# Revit family: DPD-6
name_source: partatom
category: Mechanical Equipment
revit_build: Autodesk Revit 2015 (Build: 20140606_1530(x64)
units: mm (PartAtom-declared; Revit-internal decimal feet)

## types (10) — shared parameters
Description = Drop Diffuser / Plenum
Manufacturer = United Enertech Corporation
Model = DPD-6
Type Comments = Size Options are Listed as Family Types
URL = http://unitedenertech.com

## per-type parameters (varying)
| type | B | F | Grille Height | Grille Length | T |
| DPD6-20 (8000 cfm) | 4' - 0" | 1' - 1" | 0' - 10" | 1' - 8" | 2' - 6" |
| DPD6-5 (2000 cfm) | 2' - 4" | 0' - 9" | 0' - 6" | 0' - 9" | 1' - 2" |
| DPD6-50 (20000 cfm) | 5' - 10" | 1' - 3" | 1' - 0" | 2' - 11" | 3' - 8" |
| DPD6-7.5 (3000 cfm) | 2' - 7" | 0' - 9" | 0' - 6" | 1' - 0" | 1' - 6" |
| DPD6-10 (4000 cfm) | 3' - 6" | 0' - 9" | 0' - 6" | 1' - 6" | 1' - 10" |
| DPD6-12.5 (5000 cfm) | 4' - 4" | 0' - 9" | 0' - 6" | 2' - 0" | 2' - 0" |
| DPD6-15 (6000 cfm) | 4' - 0" | 1' - 1" | 0' - 10" | 1' - 8" | 2' - 4" |
| DPD6-25 (10000 cfm) | 4' - 6" | 1' - 1" | 0' - 10" | 2' - 1" | 3' - 0" |
| DPD6-30 (12000 cfm) | 5' - 0" | 1' - 3" | 1' - 0" | 1' - 8" | 3' - 2" |
| DPD6-40 (16000 cfm) | 5' - 7" | 1' - 3" | 1' - 0" | 2' - 6" | 3' - 4" |

## geometry (parser evidence)
native form markers: Sweep x8
no freeform markers — native parametric forms only
